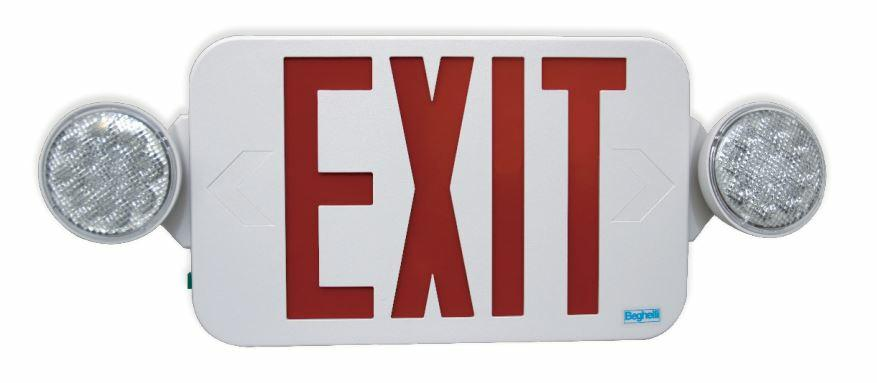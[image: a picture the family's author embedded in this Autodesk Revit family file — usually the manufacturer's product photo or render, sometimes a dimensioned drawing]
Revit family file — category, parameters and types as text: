
# Revit family: PCH-R-SA
name_source: partatom
category: Generic Models
revit_build: Autodesk Revit LT 2016 (Build: 20151007_0715(x64)
units: mm (PartAtom-declared; Revit-internal decimal feet)

## family parameters
Can host rebar = No
Cut with Voids When Loaded = No
Host = Face
Part Type = Normal
Room Calculation Point = No
Round Connector Dimension = Use Diameter
Shared = No

## types (1)
- PCH-R-SA
    Default Elevation = 4' - 0"
    Description = The PACO (PCH) combination exit and emergency unit features
performance and reliability in a small and attractive package. The
PACO (PCH) uses a rechargeable, maintenance free nickel cadmium
battery. Configured with 120/277V input. The circuit board features an
onboard solid state transformer, low voltage disconnect and brownout
protection. Red or green LEDs totaling less than 2W.
    Manufacturer = BEGHELLI
    Model = PCH-R-SA
    Type Image = PCH-R-SA PCTURE.JPG

## geometry (parser evidence)
native form markers: Sweep x19
no freeform markers — native parametric forms only
